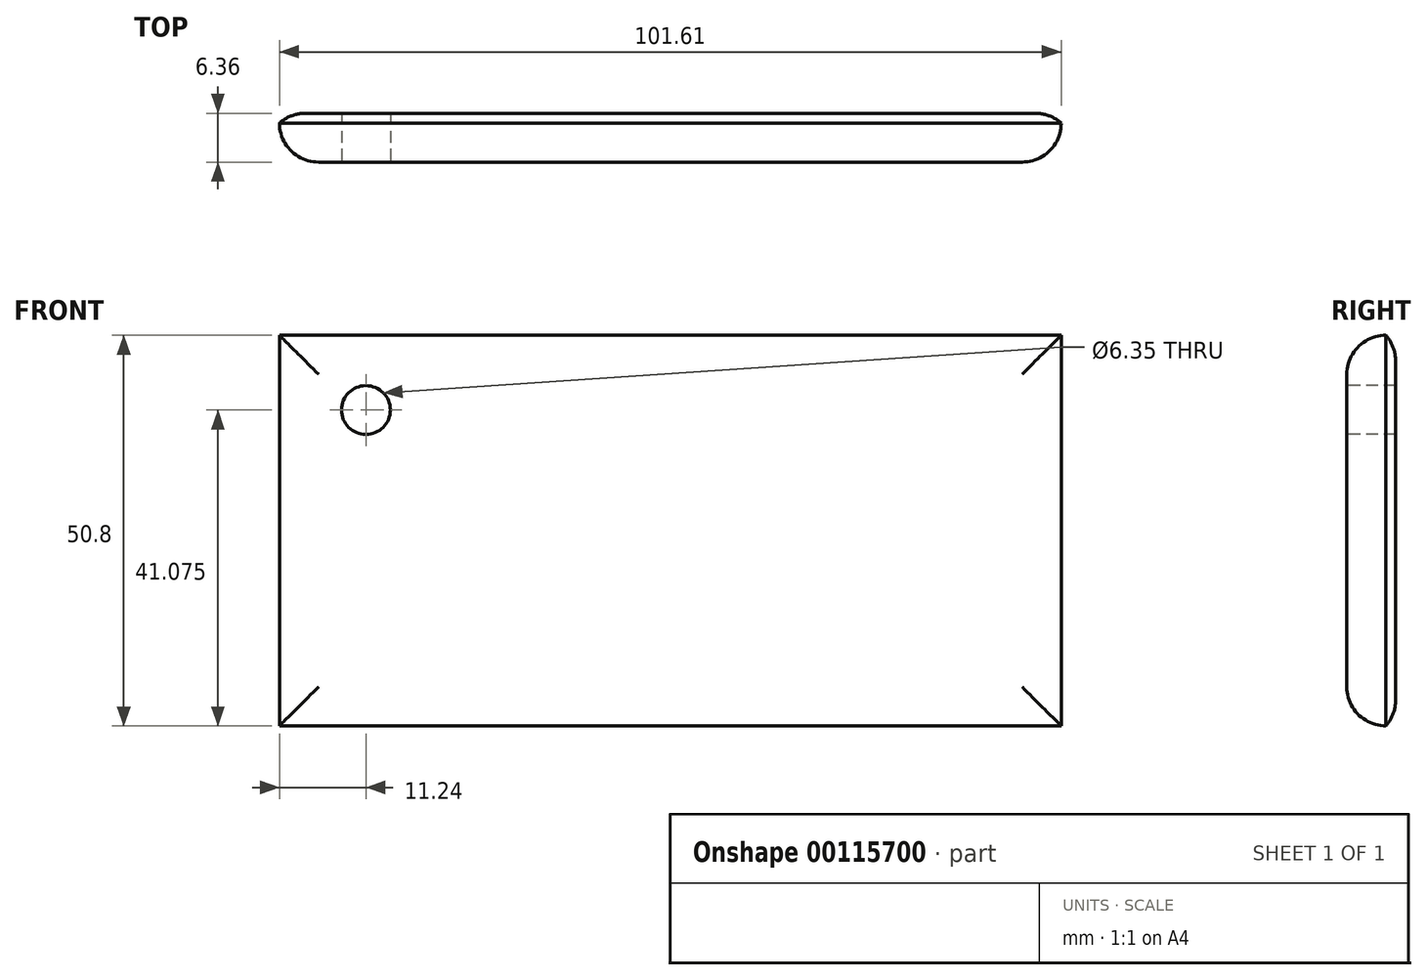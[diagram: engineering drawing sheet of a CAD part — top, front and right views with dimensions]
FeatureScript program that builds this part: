
annotation { "Feature Type Name" : "Feature", "Feature Type Description" : "" }
export const myFeature = defineFeature(function(context is Context, id is Id, definition is map)
    precondition{}
    {
        {
            var Q0;
            Q0=qCreatedBy(makeId("Front.planeOp"),FACE);
            var sketch = newSketch(context, id + "F0", { "sketchPlane" : qUnion([Q0])});
            skLineSegment(sketch, "E0", {"start": v(-49.51, 25) * mm, "end": v(52.1, 25) * mm});
            skLineSegment(sketch, "E1", {"start": v(-49.51, 25) * mm, "end": v(-49.51, -25.8) * mm});
            skLineSegment(sketch, "E2", {"start": v(-49.51, -25.8) * mm, "end": v(52.09, -25.8) * mm});
            skLineSegment(sketch, "E3", {"start": v(52.09, -25.8) * mm, "end": v(52.1, 25) * mm});
            skSolve(sketch);
        }
        {
            var Q0;
            Q0=makeQuery(id+"F0.imprint","IMPRINT",FACE,{"disambiguationData":[TD([[makeQuery(id+"F0.imprint","IMPRINT",EDGE,{"derivedFrom":sQuery(id+"F0.wireOp",EDGE,"E0")}),-1.0]])]});
            extrude(context, id + "F1", {"entities" : qUnion([Q0]), "endBound" : BoundingType.SYMMETRIC, "depth" : 6.35 * mm});
        }
        {
            var Q0;
            Q0=makeQuery(id+"F1.opExtrude","CAP_EDGE",EDGE,{"disambiguationData":[OSD([sQuery(id+"F0.wireOp",EDGE,"E1")])],"isStart":false});
            var Q1;
            Q1=makeQuery(id+"F1.opExtrude","CAP_EDGE",EDGE,{"disambiguationData":[OSD([sQuery(id+"F0.wireOp",EDGE,"E0")])],"isStart":false});
            var Q2;
            Q2=makeQuery(id+"F1.opExtrude","CAP_EDGE",EDGE,{"disambiguationData":[OSD([sQuery(id+"F0.wireOp",EDGE,"E3")])],"isStart":false});
            var Q3;
            Q3=makeQuery(id+"F1.opExtrude","CAP_EDGE",EDGE,{"disambiguationData":[OSD([sQuery(id+"F0.wireOp",EDGE,"E2")])],"isStart":false});
            fillet(context, id + "F2", {"entities" : qUnion([Q0, Q1, Q2, Q3]), "radius" : 5.08 * mm, "tangentPropagation" : true, "allowEdgeOverflow" : false});
        }
        {
            var Q0;
            Q0=makeQuery(id+"F1.opExtrude","CAP_FACE",FACE,{"disambiguationData":[OSD([sQuery(id+"F0.wireOp",EDGE,"E0"),sQuery(id+"F0.wireOp",EDGE,"E1"),sQuery(id+"F0.wireOp",EDGE,"E2"),sQuery(id+"F0.wireOp",EDGE,"E3")])],"isStart":false});
            var sketch = newSketch(context, id + "F3", { "sketchPlane" : qUnion([Q0])});
            skCircle(sketch, "E4", {"center": v(-38.27, 15.26) * mm, "radius": 3.18 * mm});
            skSolve(sketch);
        }
        {
            var Q0;
            Q0=makeQuery(id+"F3.imprint","IMPRINT",FACE,{"disambiguationData":[TD([[makeQuery(id+"F3.imprint","IMPRINT",EDGE,{"derivedFrom":sQuery(id+"F3.wireOp",EDGE,"E4")}),1.0]])]});
            extrude(context, id + "F4", {"entities" : qUnion([Q0]), "operationType" : NewBodyOperationType.REMOVE, "oppositeDirection" : true, "depth" : 25.4 * mm});
        }
        {
            var Q0;
            Q0=makeQuery(id+"F1.opExtrude","CAP_EDGE",EDGE,{"disambiguationData":[OSD([sQuery(id+"F0.wireOp",EDGE,"E0")])],"isStart":true});
            var Q1;
            Q1=makeQuery(id+"F1.opExtrude","CAP_EDGE",EDGE,{"disambiguationData":[OSD([sQuery(id+"F0.wireOp",EDGE,"E3")])],"isStart":true});
            var Q2;
            Q2=makeQuery(id+"F1.opExtrude","CAP_EDGE",EDGE,{"disambiguationData":[OSD([sQuery(id+"F0.wireOp",EDGE,"E2")])],"isStart":true});
            var Q3;
            Q3=makeQuery(id+"F1.opExtrude","CAP_EDGE",EDGE,{"disambiguationData":[OSD([sQuery(id+"F0.wireOp",EDGE,"E1")])],"isStart":true});
            fillet(context, id + "F5", {"entities" : qUnion([Q0, Q1, Q2, Q3]), "radius" : 5.08 * mm, "tangentPropagation" : true, "allowEdgeOverflow" : false});
        }
    });
